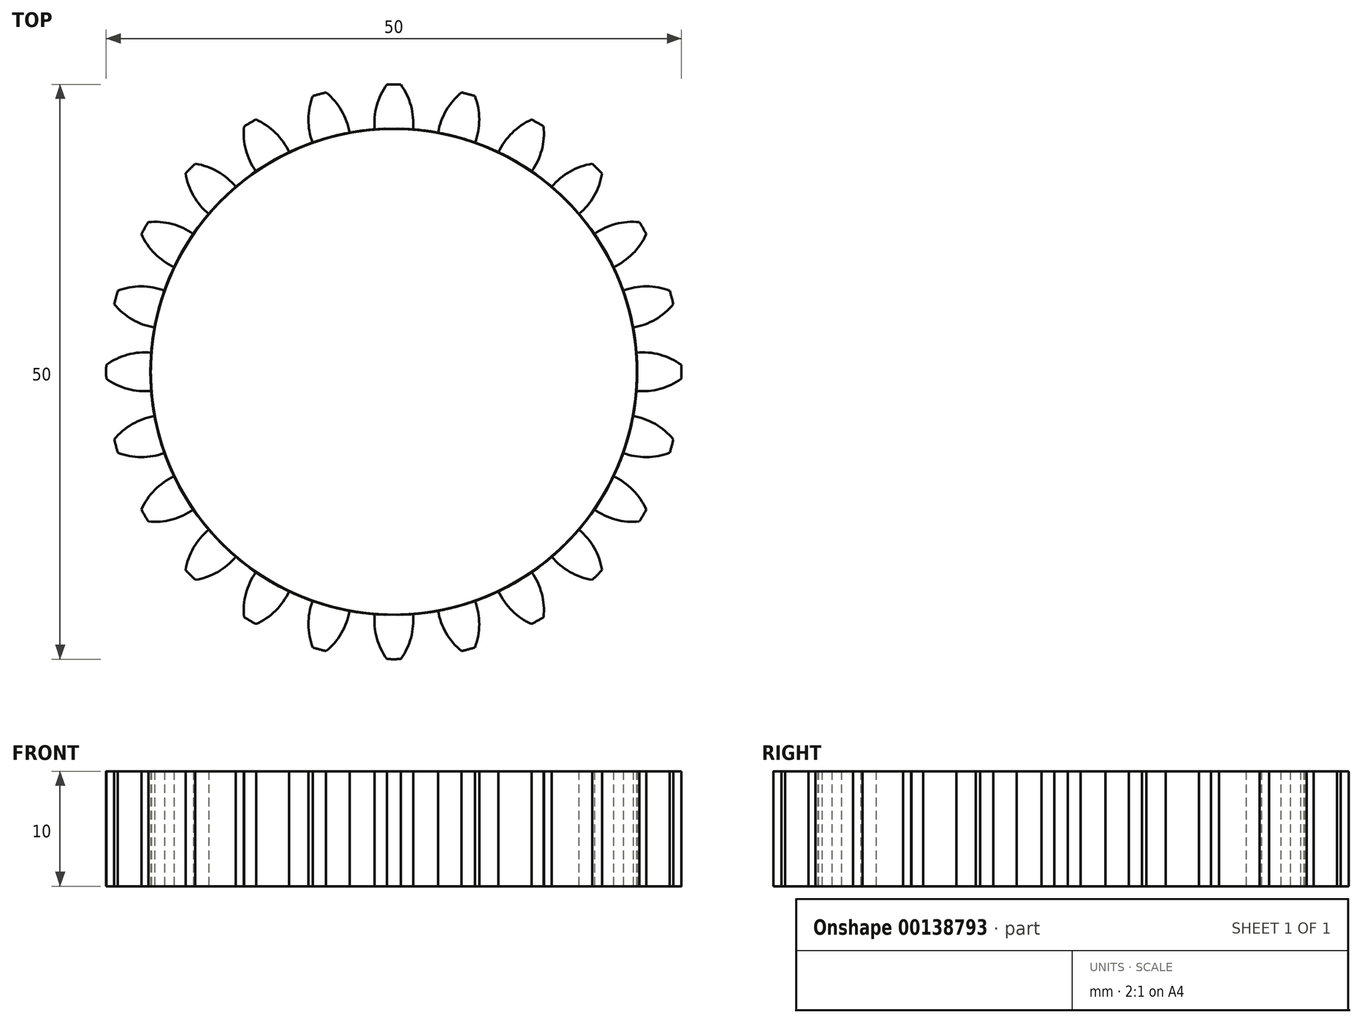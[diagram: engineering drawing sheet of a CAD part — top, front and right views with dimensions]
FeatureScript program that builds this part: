
annotation { "Feature Type Name" : "Feature", "Feature Type Description" : "" }
export const myFeature = defineFeature(function(context is Context, id is Id, definition is map)
    precondition{}
    {
        {
            var Q0;
            Q0=qCreatedBy(makeId("Top.planeOp"),FACE);
            var sketch = newSketch(context, id + "F0", { "sketchPlane" : qUnion([Q0])});
            skCircle(sketch, "E0", {"center": v(0, 0) * mm, "radius": 21.15 * mm});
            skCircle(sketch, "E1", {"center": v(0, 0) * mm, "radius": 23.1 * mm, "construction": true});
            skLineSegment(sketch, "E2", {"start": v(0, 0) * mm, "end": v(0, 25) * mm, "construction": true});
            skLineSegment(sketch, "E3", {"start": v(0, 0) * mm, "end": v(1.64, 24.95) * mm, "construction": true});
            skLineSegment(sketch, "E4", {"start": v(0, 23.1) * mm, "end": v(-32.72, 23.1) * mm, "construction": true});
            skLineSegment(sketch, "E5", {"start": v(0, 23.1) * mm, "end": v(-31.45, 11.65) * mm, "construction": true});
            skCircle(sketch, "E6", {"center": v(1.51, 23.05) * mm, "radius": 5.75 * mm, "construction": true});
            skArc(sketch, "E7", {"start": v(-2.51, 27.16) * mm, "mid": v(-8.8, 18.37) * mm, "end": v(1.67, 21.08) * mm, "construction": true});
            skArc(sketch, "E8", {"start": v(1.67, 21.08) * mm, "mid": v(1.67, 22.07) * mm, "end": v(1.51, 23.05) * mm});
            skArc(sketch, "E9", {"start": v(0.6, 25) * mm, "mid": v(-0.77, 26.34) * mm, "end": v(-2.51, 27.16) * mm, "construction": true});
            skArc(sketch, "E10", {"start": v(1.51, 23.05) * mm, "mid": v(1.15, 24.06) * mm, "end": v(0.6, 25) * mm});
            skArc(sketch, "E11", {"start": v(0, 25) * mm, "mid": v(-0.3, -25) * mm, "end": v(0.6, 25) * mm, "construction": true});
            skArc(sketch, "E12", {"start": v(0.6, 25) * mm, "mid": v(0.3, 25) * mm, "end": v(0, 25) * mm});
            skArc(sketch, "E13.MirrorCS", {"start": v(-0.6, 25) * mm, "mid": v(-0.3, 25) * mm, "end": v(0, 25) * mm});
            skArc(sketch, "E14.MirrorCS", {"start": v(-1.51, 23.05) * mm, "mid": v(-1.15, 24.06) * mm, "end": v(-0.6, 25) * mm});
            skArc(sketch, "E15.MirrorCS", {"start": v(-1.67, 21.08) * mm, "mid": v(-1.67, 22.07) * mm, "end": v(-1.51, 23.05) * mm});
            skSolve(sketch);
        }
        {
            var Q0;
            Q0=qSketchRegion(id+"F0",true);
            extrude(context, id + "F1", {"entities" : qUnion([Q0]), "depth" : (10) * mm});
        }
        {
            var Q0;
            Q0=qCreatedBy(makeId("Right.planeOp"),FACE);
            var sketch = newSketch(context, id + "F2", { "sketchPlane" : qUnion([Q0])});
            skLineSegment(sketch, "E16", {"start": v(0, 43.93) * mm, "end": v(0, 0) * mm, "construction": true});
            skSolve(sketch);
        }
        {
            var Q0;
            Q0=makeQuery(id+"F1.opExtrude","SWEPT_BODY",BODY,{"disambiguationData":[OSD([sQuery(id+"F0.wireOp",EDGE,"E0"),sQuery(id+"F0.wireOp",EDGE,"E8"),sQuery(id+"F0.wireOp",EDGE,"E10"),sQuery(id+"F0.wireOp",EDGE,"E12"),sQuery(id+"F0.wireOp",EDGE,"E13.MirrorCS"),sQuery(id+"F0.wireOp",EDGE,"E14.MirrorCS"),sQuery(id+"F0.wireOp",EDGE,"E15.MirrorCS")])]});
            var Q1;
            Q1=sQuery(id+"F2.wireOp",EDGE,"E16");
            circularPattern(context, id + "F3", {"entities" : qUnion([Q0]), "axis" : qUnion([Q1]), "angle" : 15 * degree, "instanceCount" : 24});
        }
    });
